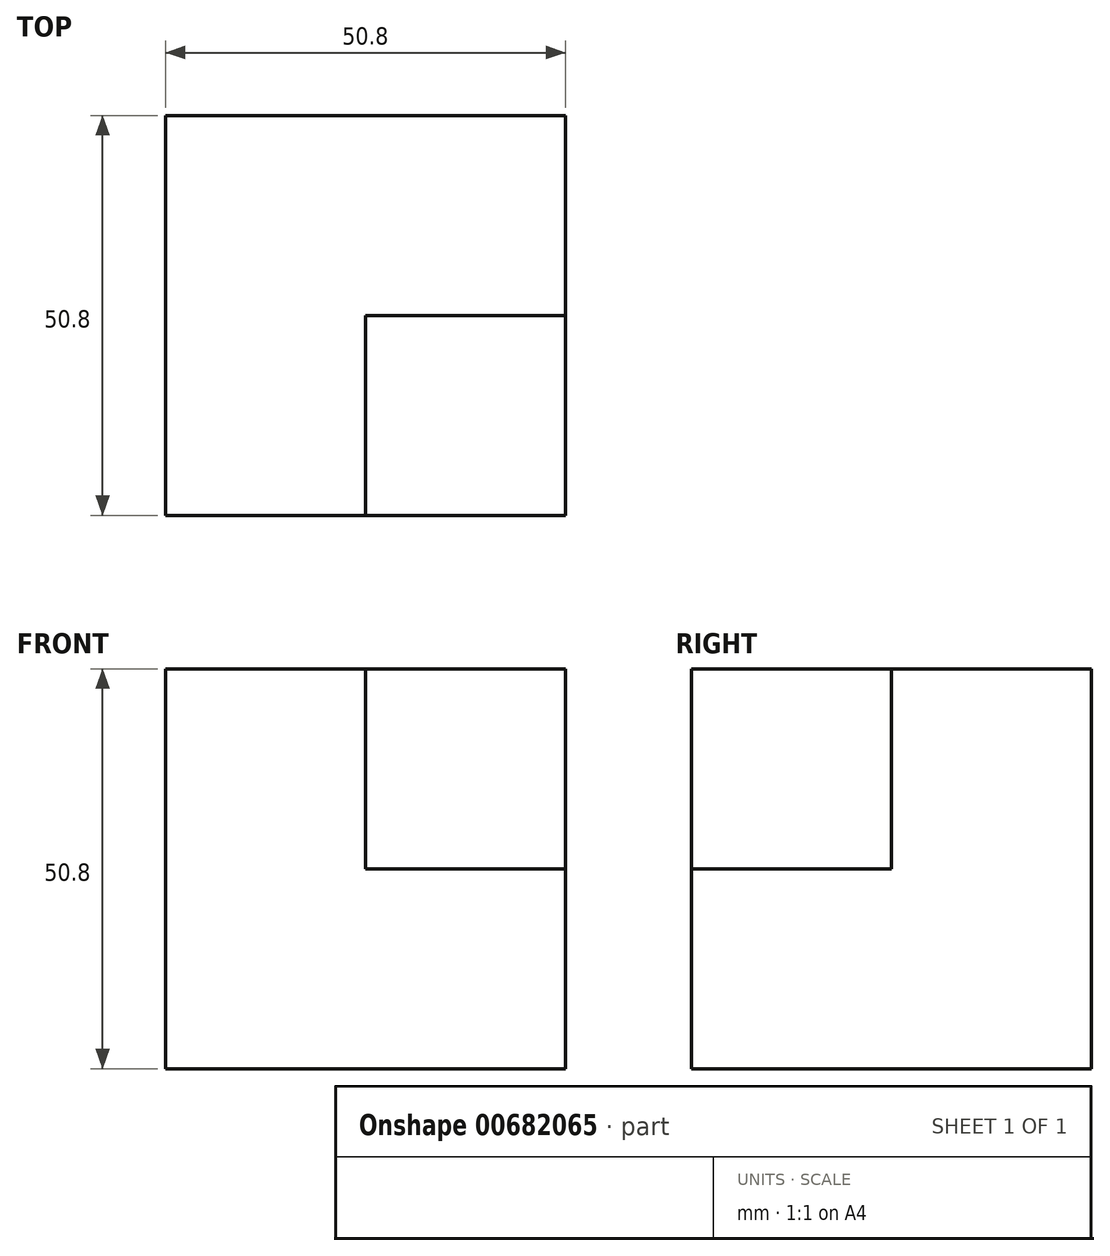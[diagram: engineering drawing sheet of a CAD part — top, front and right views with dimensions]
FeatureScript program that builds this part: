
annotation { "Feature Type Name" : "Feature", "Feature Type Description" : "" }
export const myFeature = defineFeature(function(context is Context, id is Id, definition is map)
    precondition{}
    {
        {
            var Q0;
            Q0=qCreatedBy(makeId("Front.planeOp"),FACE);
            var sketch = newSketch(context, id + "F0", { "sketchPlane" : qUnion([Q0])});
            skLineSegment(sketch, "E0.bottom", {"start": v(0.28, 17.1) * mm, "end": v(51.08, 17.1) * mm});
            skLineSegment(sketch, "E0.top", {"start": v(0.28, -33.7) * mm, "end": v(51.08, -33.7) * mm});
            skLineSegment(sketch, "E0.left", {"start": v(0.28, 17.1) * mm, "end": v(0.28, -33.7) * mm});
            skLineSegment(sketch, "E0.right", {"start": v(51.08, 17.1) * mm, "end": v(51.08, -33.7) * mm});
            skSolve(sketch);
        }
        {
            var Q0;
            Q0 = qSketchRegion(id + "F0", true);
            extrude(context, id + "F1", {"entities" : qUnion([Q0]), "depth" : 50.8 * mm, "offsetDistance" : 25.4 * mm});
        }
        {
            var Q0;
            Q0=qCreatedBy(makeId("Front.planeOp"),FACE);
            var sketch = newSketch(context, id + "F2", { "sketchPlane" : qUnion([Q0])});
            skLineSegment(sketch, "E1.bottom", {"start": v(50.7, 16.7) * mm, "end": v(25.3, 16.7) * mm});
            skLineSegment(sketch, "E1.top", {"start": v(50.7, -8.7) * mm, "end": v(25.3, -8.7) * mm});
            skLineSegment(sketch, "E1.left", {"start": v(50.7, 16.7) * mm, "end": v(50.7, -8.7) * mm});
            skLineSegment(sketch, "E1.right", {"start": v(25.3, 16.7) * mm, "end": v(25.3, -8.7) * mm});
            skSolve(sketch);
        }
        {
            var Q0;
            Q0 = qSketchRegion(id + "F2", true);
            extrude(context, id + "F3", {"entities" : qUnion([Q0]), "operationType" : NewBodyOperationType.REMOVE, "oppositeDirection" : true, "depth" : 25.4 * mm, "offsetDistance" : 25.4 * mm});
        }
        {
            var Q0;
            Q0=makeQuery(id+"F1.opExtrude","CAP_FACE",FACE,{"disambiguationData":[OSD([sQuery(id+"F0.wireOp",EDGE,"E0.bottom"),sQuery(id+"F0.wireOp",EDGE,"E0.top"),sQuery(id+"F0.wireOp",EDGE,"E0.left"),sQuery(id+"F0.wireOp",EDGE,"E0.right")])],"isStart":false});
            var sketch = newSketch(context, id + "F4", { "sketchPlane" : qUnion([Q0])});
            skLineSegment(sketch, "E2.bottom", {"start": v(51.08, 17.1) * mm, "end": v(25.68, 17.1) * mm});
            skLineSegment(sketch, "E2.top", {"start": v(51.08, -8.3) * mm, "end": v(25.68, -8.3) * mm});
            skLineSegment(sketch, "E2.left", {"start": v(51.08, 17.1) * mm, "end": v(51.08, -8.3) * mm});
            skLineSegment(sketch, "E2.right", {"start": v(25.68, 17.1) * mm, "end": v(25.68, -8.3) * mm});
            skSolve(sketch);
        }
        {
            var Q0;
            Q0 = qSketchRegion(id + "F4", true);
            extrude(context, id + "F5", {"entities" : qUnion([Q0]), "operationType" : NewBodyOperationType.REMOVE, "oppositeDirection" : true, "depth" : 25.4 * mm, "offsetDistance" : 25.4 * mm});
        }
    });
